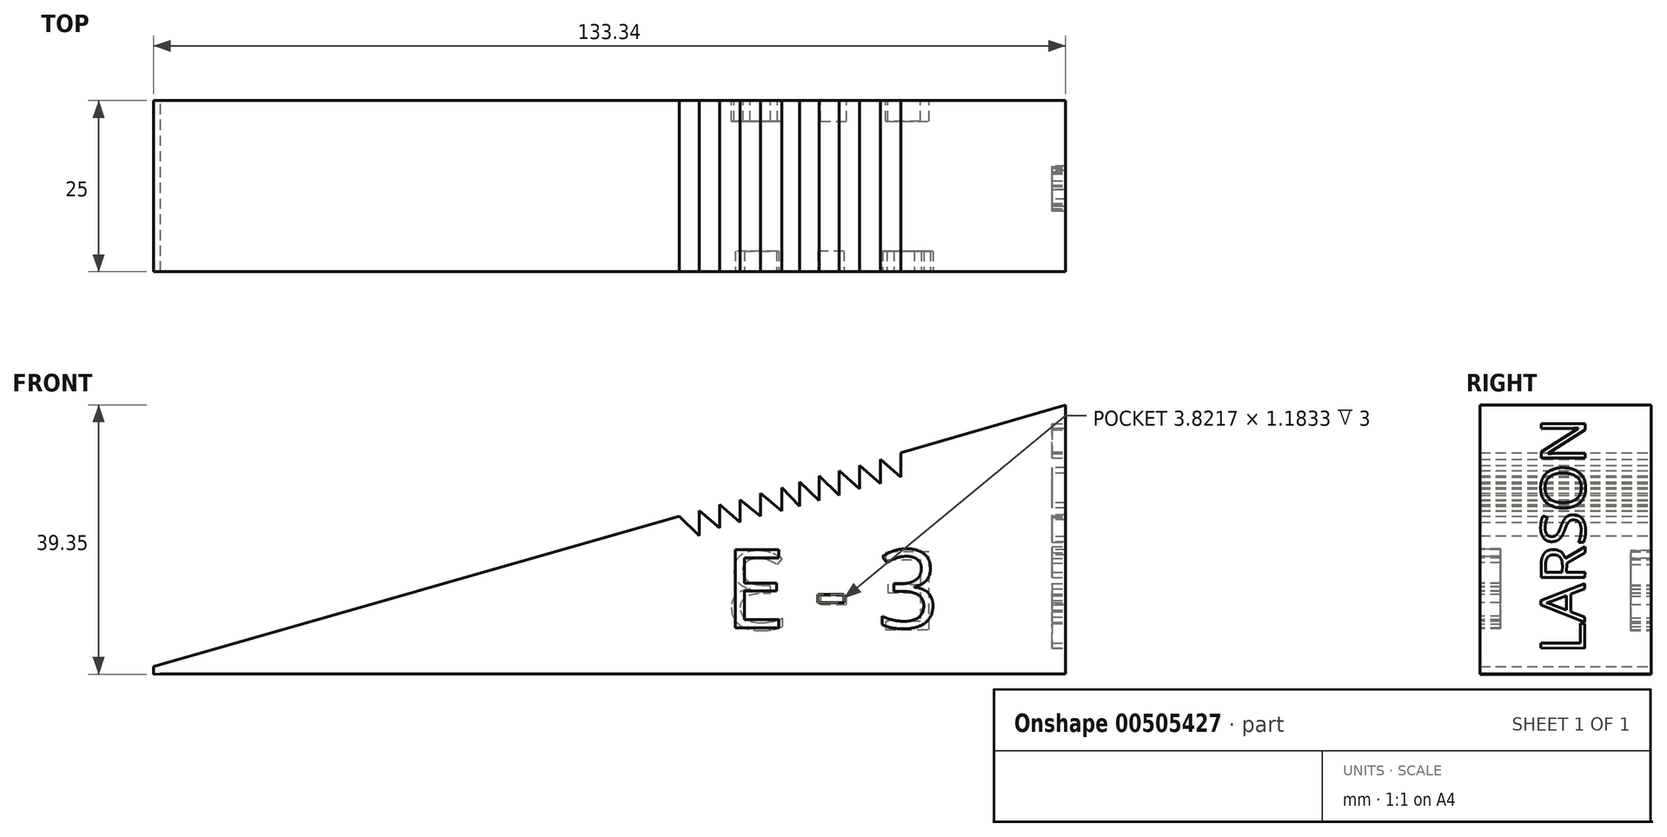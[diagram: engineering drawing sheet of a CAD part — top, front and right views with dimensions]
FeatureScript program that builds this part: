
annotation { "Feature Type Name" : "Feature", "Feature Type Description" : "" }
export const myFeature = defineFeature(function(context is Context, id is Id, definition is map)
    precondition{}
    {
        {
            var Q0;
            Q0=qCreatedBy(makeId("Front.planeOp"),FACE);
            var sketch = newSketch(context, id + "F0", { "sketchPlane" : qUnion([Q0])});
            skLineSegment(sketch, "E0", {"start": v(-57.96, -21.36) * mm, "end": v(74.33, -21.36) * mm});
            skLineSegment(sketch, "E1", {"start": v(74.33, -21.36) * mm, "end": v(74.33, 17.97) * mm});
            skLineSegment(sketch, "E2", {"start": v(74.33, 17.97) * mm, "end": v(50.24, 11) * mm});
            skLineSegment(sketch, "E3", {"start": v(50.24, 11) * mm, "end": v(50.24, 7.43) * mm});
            skLineSegment(sketch, "E4", {"start": v(50.24, 7.43) * mm, "end": v(47.23, 10.07) * mm});
            skLineSegment(sketch, "E5", {"start": v(47.23, 10.07) * mm, "end": v(47.23, 6.5) * mm});
            skLineSegment(sketch, "E6", {"start": v(47.23, 6.5) * mm, "end": v(44.22, 9.13) * mm});
            skLineSegment(sketch, "E7", {"start": v(44.22, 9.13) * mm, "end": v(44.22, 5.74) * mm});
            skLineSegment(sketch, "E8", {"start": v(44.22, 5.74) * mm, "end": v(41.2, 8.37) * mm});
            skLineSegment(sketch, "E9", {"start": v(41.2, 8.37) * mm, "end": v(41.2, 4.8) * mm});
            skLineSegment(sketch, "E10", {"start": v(41.2, 4.8) * mm, "end": v(38.28, 7.6) * mm});
            skLineSegment(sketch, "E11", {"start": v(38.28, 7.6) * mm, "end": v(38.28, 4) * mm});
            skLineSegment(sketch, "E12", {"start": v(38.28, 4) * mm, "end": v(35.43, 6.76) * mm});
            skLineSegment(sketch, "E13", {"start": v(35.43, 6.76) * mm, "end": v(35.43, 3.16) * mm});
            skLineSegment(sketch, "E14", {"start": v(35.43, 3.16) * mm, "end": v(32.83, 5.92) * mm});
            skLineSegment(sketch, "E15", {"start": v(32.83, 5.92) * mm, "end": v(32.83, 2.49) * mm});
            skLineSegment(sketch, "E16", {"start": v(32.83, 2.49) * mm, "end": v(29.73, 5.08) * mm});
            skLineSegment(sketch, "E17", {"start": v(29.73, 5.08) * mm, "end": v(29.73, 1.73) * mm});
            skLineSegment(sketch, "E18", {"start": v(29.73, 1.73) * mm, "end": v(26.71, 4.16) * mm});
            skLineSegment(sketch, "E19", {"start": v(26.71, 4.16) * mm, "end": v(26.71, 0.8) * mm});
            skLineSegment(sketch, "E20", {"start": v(26.71, 0.8) * mm, "end": v(23.78, 3.4) * mm});
            skLineSegment(sketch, "E21", {"start": v(23.78, 3.4) * mm, "end": v(23.78, 0) * mm});
            skLineSegment(sketch, "E22", {"start": v(23.78, 0) * mm, "end": v(20.76, 2.57) * mm});
            skLineSegment(sketch, "E23", {"start": v(20.76, 2.57) * mm, "end": v(20.76, -1.12) * mm});
            skLineSegment(sketch, "E24", {"start": v(20.76, -1.12) * mm, "end": v(17.83, 1.73) * mm});
            skLineSegment(sketch, "E25", {"start": v(17.83, 1.73) * mm, "end": v(-59.01, -20.26) * mm});
            skLineSegment(sketch, "E26", {"start": v(-59.01, -20.26) * mm, "end": v(-59.01, -21.38) * mm});
            skLineSegment(sketch, "E27", {"start": v(-59.01, -21.38) * mm, "end": v(-57.96, -21.36) * mm});
            skSolve(sketch);
        }
        {
            var Q0;
            Q0=makeQuery(id+"F0.imprint","IMPRINT",FACE,{"disambiguationData":[TD([[makeQuery(id+"F0.imprint","IMPRINT",EDGE,{"derivedFrom":sQuery(id+"F0.wireOp",EDGE,"E0")}),1.0]])]});
            extrude(context, id + "F1", {"entities" : qUnion([Q0]), "depth" : 25 * mm});
        }
        {
            var Q0;
            Q0=makeQuery(id+"F1.opExtrude","CAP_FACE",FACE,{"disambiguationData":[OSD([sQuery(id+"F0.wireOp",EDGE,"E0"),sQuery(id+"F0.wireOp",EDGE,"E1"),sQuery(id+"F0.wireOp",EDGE,"E2"),sQuery(id+"F0.wireOp",EDGE,"E3"),sQuery(id+"F0.wireOp",EDGE,"E4"),sQuery(id+"F0.wireOp",EDGE,"E5"),sQuery(id+"F0.wireOp",EDGE,"E6"),sQuery(id+"F0.wireOp",EDGE,"E7"),sQuery(id+"F0.wireOp",EDGE,"E8"),sQuery(id+"F0.wireOp",EDGE,"E9"),sQuery(id+"F0.wireOp",EDGE,"E10"),sQuery(id+"F0.wireOp",EDGE,"E11"),sQuery(id+"F0.wireOp",EDGE,"E12"),sQuery(id+"F0.wireOp",EDGE,"E13"),sQuery(id+"F0.wireOp",EDGE,"E14"),sQuery(id+"F0.wireOp",EDGE,"E15"),sQuery(id+"F0.wireOp",EDGE,"E16"),sQuery(id+"F0.wireOp",EDGE,"E17"),sQuery(id+"F0.wireOp",EDGE,"E18"),sQuery(id+"F0.wireOp",EDGE,"E19"),sQuery(id+"F0.wireOp",EDGE,"E20"),sQuery(id+"F0.wireOp",EDGE,"E21"),sQuery(id+"F0.wireOp",EDGE,"E22"),sQuery(id+"F0.wireOp",EDGE,"E23"),sQuery(id+"F0.wireOp",EDGE,"E24"),sQuery(id+"F0.wireOp",EDGE,"E25"),sQuery(id+"F0.wireOp",EDGE,"E26"),sQuery(id+"F0.wireOp",EDGE,"E27")])],"isStart":false});
            var sketch = newSketch(context, id + "F2", { "sketchPlane" : qUnion([Q0])});
            skText(sketch, "E28", { "text": "E - 3", "fontName": "OpenSans-Regular.ttf"});
            const initialGuessF2  = {"E28": [0.02446, -0.01458, 1, 0, 0.01148]};
            skSetInitialGuess(sketch, initialGuessF2);
            skSolve(sketch);
        }
        {
            var Q0;
            Q0=makeQuery(id+"F1.opExtrude","CAP_FACE",FACE,{"disambiguationData":[OSD([sQuery(id+"F0.wireOp",EDGE,"E0"),sQuery(id+"F0.wireOp",EDGE,"E1"),sQuery(id+"F0.wireOp",EDGE,"E2"),sQuery(id+"F0.wireOp",EDGE,"E3"),sQuery(id+"F0.wireOp",EDGE,"E4"),sQuery(id+"F0.wireOp",EDGE,"E5"),sQuery(id+"F0.wireOp",EDGE,"E6"),sQuery(id+"F0.wireOp",EDGE,"E7"),sQuery(id+"F0.wireOp",EDGE,"E8"),sQuery(id+"F0.wireOp",EDGE,"E9"),sQuery(id+"F0.wireOp",EDGE,"E10"),sQuery(id+"F0.wireOp",EDGE,"E11"),sQuery(id+"F0.wireOp",EDGE,"E12"),sQuery(id+"F0.wireOp",EDGE,"E13"),sQuery(id+"F0.wireOp",EDGE,"E14"),sQuery(id+"F0.wireOp",EDGE,"E15"),sQuery(id+"F0.wireOp",EDGE,"E16"),sQuery(id+"F0.wireOp",EDGE,"E17"),sQuery(id+"F0.wireOp",EDGE,"E18"),sQuery(id+"F0.wireOp",EDGE,"E19"),sQuery(id+"F0.wireOp",EDGE,"E20"),sQuery(id+"F0.wireOp",EDGE,"E21"),sQuery(id+"F0.wireOp",EDGE,"E22"),sQuery(id+"F0.wireOp",EDGE,"E23"),sQuery(id+"F0.wireOp",EDGE,"E24"),sQuery(id+"F0.wireOp",EDGE,"E25"),sQuery(id+"F0.wireOp",EDGE,"E26"),sQuery(id+"F0.wireOp",EDGE,"E27")])],"isStart":true});
            var sketch = newSketch(context, id + "F3", { "sketchPlane" : qUnion([Q0])});
            skText(sketch, "E29", { "text": "E - 3", "fontName": "OpenSans-Regular.ttf"});
            const initialGuessF3  = {"E29": [-0.05595, -0.01485, 1, 0, 0.01148]};
            skSetInitialGuess(sketch, initialGuessF3);
            skSolve(sketch);
        }
        {
            var Q0;
            Q0=qSketchRegion(id+"F2",true);
            extrude(context, id + "F4", {"entities" : qUnion([Q0]), "operationType" : NewBodyOperationType.REMOVE, "oppositeDirection" : true, "depth" : 3 * mm});
        }
        {
            var Q0;
            Q0=qSketchRegion(id+"F3",true);
            extrude(context, id + "F5", {"entities" : qUnion([Q0]), "operationType" : NewBodyOperationType.REMOVE, "oppositeDirection" : true, "depth" : 3 * mm});
        }
        {
            var Q0;
            Q0=makeQuery(id+"F1.opExtrude","SWEPT_FACE",FACE,{"disambiguationData":[OSD([sQuery(id+"F0.wireOp",EDGE,"E1")])]});
            var sketch = newSketch(context, id + "F6", { "sketchPlane" : qUnion([Q0])});
            skText(sketch, "E30", { "text": "LARSON", "fontName": "OpenSans-Regular.ttf"});
            const initialGuessF6  = {"E30": [-0.0097, -0.01844, 0.00203, 1, 0.00646]};
            skSetInitialGuess(sketch, initialGuessF6);
            skSolve(sketch);
        }
        {
            var Q0;
            Q0=qSketchRegion(id+"F6",true);
            extrude(context, id + "F7", {"entities" : qUnion([Q0]), "operationType" : NewBodyOperationType.REMOVE, "oppositeDirection" : true, "depth" : 2 * mm});
        }
    });
